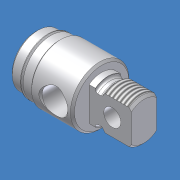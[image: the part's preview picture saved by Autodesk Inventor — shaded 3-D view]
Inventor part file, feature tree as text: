
AUTODESK INVENTOR PART (.ipt)
format: ipt  version: 2012 (Build 160160000, 160)  size: 265,728 bytes
history: native  units: mm (DEFAULTED — no unit token found)
features: other x155, sketch x7, revolve x5, extrude x2, thread x1
ambient origin geometry x8: Origin, YZ Plane, XZ Plane, XY Plane, X Axis, Y Axis, Z Axis, Center Point
bodies: Solid1 (feature_tree)
feature tree (170):
  other  "04P0010_rear_head"
  revolve  "Revolution1"  Angle=360.0deg
  revolve  "Revolution2"  [1 undecoded]
  thread  "Thread1"  [1 undecoded]
  extrude  "Extrusion1"  TaperAngle=360.0deg  [1 undecoded]
  revolve  "Revolution3"  [1 undecoded]
  revolve  "Revolution4"  [1 undecoded]
  revolve  "Revolution5"  [1 undecoded]
  extrude  "Extrusion2"  [1 undecoded]
  other  "c1_XY"
  other  "c1_YZ"
  other  "c1_ZX"
  other  "c1_X"
  other  "c1_Y"
  other  "c1_Z"
  other  "c1_Center"
  other  "cc1_XY"
  other  "cc1_YZ"
  other  "cc1_ZX"
  other  "cc1_X"
  other  "cc1_Y"
  other  "cc1_Z"
  other  "cc1_Center"
  other  "c2_XY"
  other  "c2_YZ"
  other  "c2_ZX"
  other  "c2_X"
  other  "c2_Y"
  other  "c2_Z"
  other  "c2_Center"
  other  "cc2_XY"
  other  "cc2_YZ"
  other  "cc2_ZX"
  other  "cc2_X"
  other  "cc2_Y"
  other  "cc2_Z"
  other  "cc2_Center"
  other  "to_tube_XY"
  other  "to_tube_YZ"
  other  "to_tube_ZX"
  other  "to_tube_X"
  other  "to_tube_Y"
  other  "to_tube_Z"
  other  "to_tube_Center"
  other  "to_nut_XY"
  other  "to_nut_YZ"
  other  "to_nut_ZX"
  other  "to_nut_X"
  other  "to_nut_Y"
  other  "to_nut_Z"
  other  "to_nut_Center"
  other  "lovra1_XY"
  other  "lovra1_YZ"
  other  "lovra1_ZX"
  other  "lovra1_X"
  other  "lovra1_Y"
  other  "lovra1_Z"
  other  "lovra1_Center"
  other  "lovra2_XY"
  other  "lovra2_YZ"
  other  "lovra2_ZX"
  other  "lovra2_X"
  other  "lovra2_Y"
  other  "lovra2_Z"
  other  "lovra2_Center"
  other  "lovra3_XY"
  other  "lovra3_YZ"
  other  "lovra3_ZX"
  other  "lovra3_X"
  other  "lovra3_Y"
  other  "lovra3_Z"
  other  "lovra3_Center"
  other  "to_pin_XY"
  other  "to_pin_YZ"
  other  "to_pin_ZX"
  other  "to_pin_X"
  other  "to_pin_Y"
  other  "to_pin_Z"
  other  "to_pin_Center"
  other  "olen_XY"
  other  "olen_YZ"
  other  "olen_ZX"
  other  "olen_X"
  other  "olen_Y"
  other  "olen_Z"
  other  "olen_Center"
  other  "thd1_XY"
  other  "thd1_YZ"
  other  "thd1_ZX"
  other  "thd1_X"
  other  "thd1_Y"
  other  "thd1_Z"
  other  "thd1_Center"
  other  "p1_XY"
  other  "p1_YZ"
  other  "p1_ZX"
  other  "p1_X"
  other  "p1_Y"
  other  "p1_Z"
  other  "p1_Center"
  other  "thd2_XY"
  other  "thd2_YZ"
  other  "thd2_ZX"
  other  "thd2_X"
  other  "thd2_Y"
  other  "thd2_Z"
  other  "thd2_Center"
  other  "p2_XY"
  other  "p2_YZ"
  other  "p2_ZX"
  other  "p2_X"
  other  "p2_Y"
  other  "p2_Z"
  other  "p2_Center"
  other  "port2_XY"
  other  "port2_YZ"
  other  "port2_ZX"
  other  "port2_X"
  other  "port2_Y"
  other  "port2_Z"
  other  "port2_Center"
  other  "port_XY"
  other  "port_YZ"
  other  "port_ZX"
  other  "port_X"
  other  "port_Y"
  other  "port_Z"
  other  "port_Center"
  other  "1_XY"
  other  "1_YZ"
  other  "1_ZX"
  other  "1_X"
  other  "1_Y"
  other  "1_Z"
  other  "1_Center"
  other  "lovra21_XY"
  other  "lovra21_YZ"
  other  "lovra21_ZX"
  other  "lovra21_X"
  other  "lovra21_Y"
  other  "lovra21_Z"
  other  "lovra21_Center"
  other  "lovra22_XY"
  other  "lovra22_YZ"
  other  "lovra22_ZX"
  other  "lovra22_X"
  other  "lovra22_Y"
  other  "lovra22_Z"
  other  "lovra22_Center"
  other  "to_screw_XY"
  other  "to_screw_YZ"
  other  "to_screw_ZX"
  other  "to_screw_X"
  other  "to_screw_Y"
  other  "to_screw_Z"
  other  "to_screw_Center"
  other  "to_mounting_bracket_XY"
  other  "to_mounting_bracket_YZ"
  other  "to_mounting_bracket_ZX"
  other  "to_mounting_bracket_X"
  other  "to_mounting_bracket_Y"
  other  "to_mounting_bracket_Z"
  other  "to_mounting_bracket_Center"
  sketch  "Sketch_8"  dims[d0=360.0deg d1=360.0deg]
  sketch  "Sketch_15"  dims[d9=14.19225mm d10=0.0mm]
  sketch  "Sketch_9"  dims[d2=9.008135mm d3=0.0mm d4=15.875mm d5=0.0mm d6=360.0deg]
  sketch  "Sketch_13"  dims[d7=360.0deg d8=360.0deg]
  sketch  "Sketch_19"
  sketch  "Sketch_24"
  sketch  "Sketch_43"
note: 7 required parameter values undecoded (feature->parameter linkage not recoverable at this tier; creation-order binding heuristic only, values carry confidence <= 0.55)